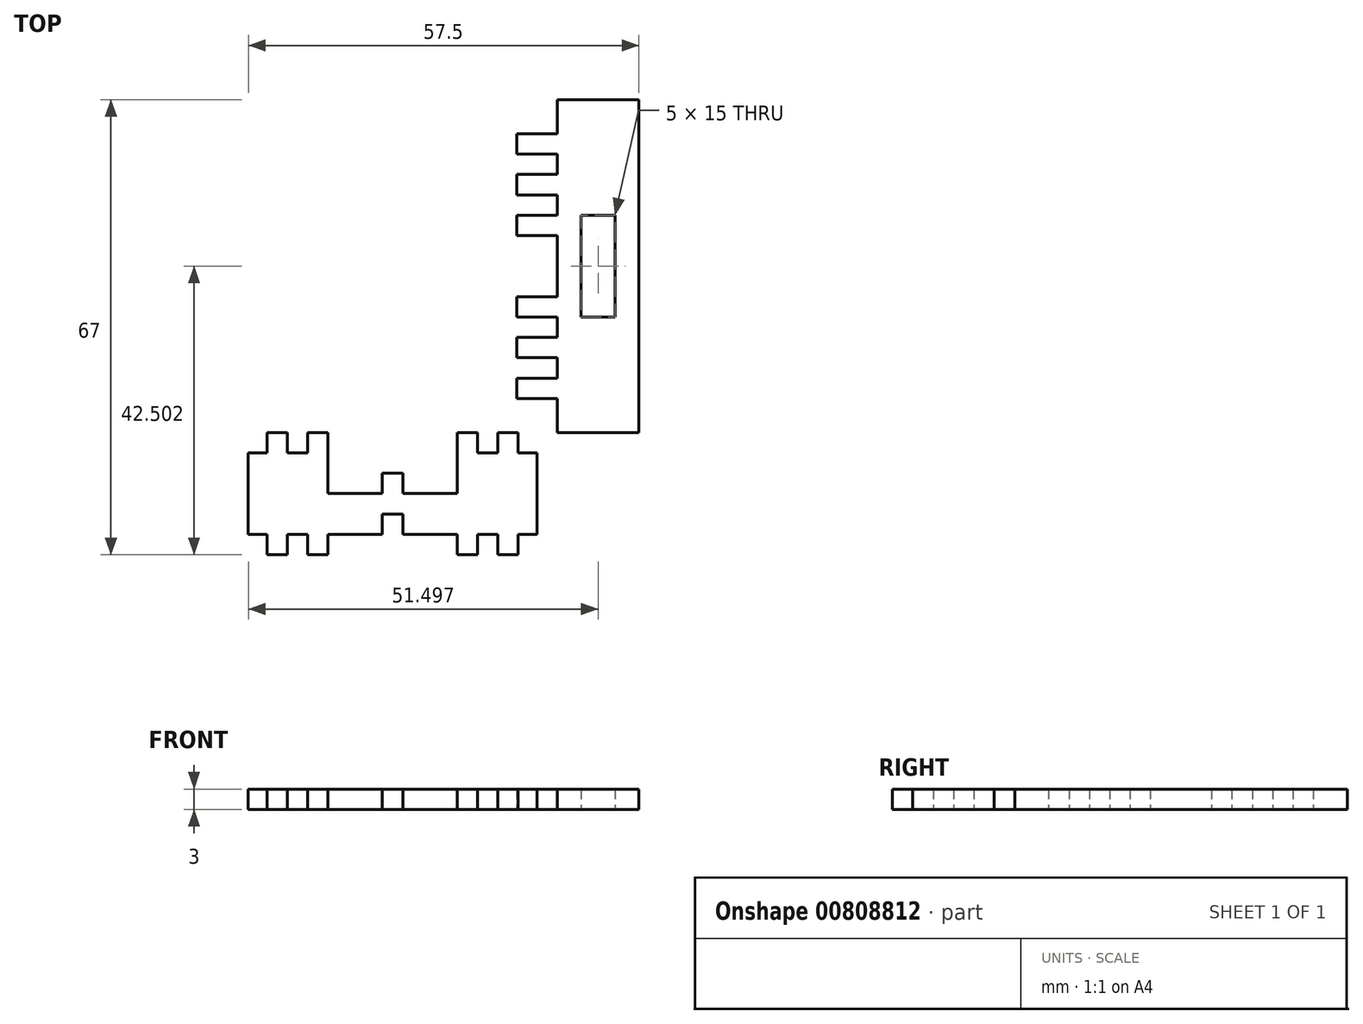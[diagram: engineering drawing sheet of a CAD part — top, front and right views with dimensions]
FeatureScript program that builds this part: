
annotation { "Feature Type Name" : "Feature", "Feature Type Description" : "" }
export const myFeature = defineFeature(function(context is Context, id is Id, definition is map)
    precondition{}
    {
        {
            var Q0;
            Q0=qCreatedBy(makeId("Top.planeOp"),FACE);
            var sketch = newSketch(context, id + "F0", { "sketchPlane" : qUnion([Q0])});
            skLineSegment(sketch, "E0.bottom", {"start": v(20.27, -26.13) * mm, "end": v(-22.23, -26.13) * mm});
            skLineSegment(sketch, "E0.top", {"start": v(20.27, 28.87) * mm, "end": v(-22.23, 28.87) * mm});
            skLineSegment(sketch, "E0.left", {"start": v(20.27, -26.13) * mm, "end": v(20.27, 28.87) * mm});
            skLineSegment(sketch, "E0.right", {"start": v(-22.23, -26.13) * mm, "end": v(-22.23, 28.87) * mm});
            skPoint(sketch, "E0.middle", {"position": v(-0.98, 1.37) * mm});
            skLineSegment(sketch, "E1.bottom", {"start": v(-19.23, -0.13) * mm, "end": v(-25.23, -0.13) * mm});
            skLineSegment(sketch, "E1.top", {"start": v(-19.23, 2.87) * mm, "end": v(-25.23, 2.87) * mm});
            skLineSegment(sketch, "E1.left", {"start": v(-19.23, -0.13) * mm, "end": v(-19.23, 2.87) * mm});
            skLineSegment(sketch, "E1.right", {"start": v(-25.23, -0.13) * mm, "end": v(-25.23, 2.87) * mm});
            skPoint(sketch, "E1.middle", {"position": v(-22.23, 1.37) * mm});
            skLineSegment(sketch, "E2.bottom", {"start": v(23.27, -0.13) * mm, "end": v(17.27, -0.13) * mm});
            skLineSegment(sketch, "E2.top", {"start": v(23.27, 2.87) * mm, "end": v(17.27, 2.87) * mm});
            skLineSegment(sketch, "E2.left", {"start": v(23.27, -0.13) * mm, "end": v(23.27, 2.87) * mm});
            skLineSegment(sketch, "E2.right", {"start": v(17.27, -0.13) * mm, "end": v(17.27, 2.87) * mm});
            skPoint(sketch, "E2.middle", {"position": v(20.27, 1.37) * mm});
            skLineSegment(sketch, "E3.bottom", {"start": v(0.52, -29.13) * mm, "end": v(-2.48, -29.13) * mm});
            skLineSegment(sketch, "E3.top", {"start": v(0.52, -23.13) * mm, "end": v(-2.48, -23.13) * mm});
            skLineSegment(sketch, "E3.left", {"start": v(0.52, -29.13) * mm, "end": v(0.52, -23.13) * mm});
            skLineSegment(sketch, "E3.right", {"start": v(-2.48, -29.13) * mm, "end": v(-2.48, -23.13) * mm});
            skPoint(sketch, "E3.middle", {"position": v(-0.98, -26.13) * mm});
            skLineSegment(sketch, "E4.bottom", {"start": v(0.52, 25.87) * mm, "end": v(-2.48, 25.87) * mm});
            skLineSegment(sketch, "E4.top", {"start": v(0.52, 31.87) * mm, "end": v(-2.48, 31.87) * mm});
            skLineSegment(sketch, "E4.left", {"start": v(0.52, 25.87) * mm, "end": v(0.52, 31.87) * mm});
            skLineSegment(sketch, "E4.right", {"start": v(-2.48, 25.87) * mm, "end": v(-2.48, 31.87) * mm});
            skPoint(sketch, "E4.middle", {"position": v(-0.98, 28.87) * mm});
            skLineSegment(sketch, "E5.bottom", {"start": v(-10.68, -18.58) * mm, "end": v(8.72, -18.58) * mm});
            skLineSegment(sketch, "E5.top", {"start": v(-10.68, 21.32) * mm, "end": v(8.72, 21.32) * mm});
            skLineSegment(sketch, "E5.left", {"start": v(-10.68, -18.58) * mm, "end": v(-10.68, 21.32) * mm});
            skLineSegment(sketch, "E5.right", {"start": v(8.72, -18.58) * mm, "end": v(8.72, 21.32) * mm});
            skLineSegment(sketch, "E6.bottom", {"start": v(-19.23, -6.13) * mm, "end": v(-25.23, -6.13) * mm});
            skLineSegment(sketch, "E6.top", {"start": v(-19.23, -3.13) * mm, "end": v(-25.23, -3.13) * mm});
            skLineSegment(sketch, "E6.left", {"start": v(-19.23, -6.13) * mm, "end": v(-19.23, -3.13) * mm});
            skLineSegment(sketch, "E6.right", {"start": v(-25.23, -6.13) * mm, "end": v(-25.23, -3.13) * mm});
            skPoint(sketch, "E6.middle", {"position": v(-22.23, -4.63) * mm});
            skLineSegment(sketch, "E7.bottom", {"start": v(-19.23, 5.87) * mm, "end": v(-25.23, 5.87) * mm});
            skLineSegment(sketch, "E7.top", {"start": v(-19.23, 8.87) * mm, "end": v(-25.23, 8.87) * mm});
            skLineSegment(sketch, "E7.left", {"start": v(-19.23, 5.87) * mm, "end": v(-19.23, 8.87) * mm});
            skLineSegment(sketch, "E7.right", {"start": v(-25.23, 5.87) * mm, "end": v(-25.23, 8.87) * mm});
            skPoint(sketch, "E7.middle", {"position": v(-22.23, 7.37) * mm});
            skLineSegment(sketch, "E8.bottom", {"start": v(-19.23, 11.87) * mm, "end": v(-25.23, 11.87) * mm});
            skLineSegment(sketch, "E8.top", {"start": v(-19.23, 14.87) * mm, "end": v(-25.23, 14.87) * mm});
            skLineSegment(sketch, "E8.left", {"start": v(-19.23, 11.87) * mm, "end": v(-19.23, 14.87) * mm});
            skLineSegment(sketch, "E8.right", {"start": v(-25.23, 11.87) * mm, "end": v(-25.23, 14.87) * mm});
            skPoint(sketch, "E8.middle", {"position": v(-22.23, 13.37) * mm});
            skLineSegment(sketch, "E9.bottom", {"start": v(-19.23, -12.13) * mm, "end": v(-25.23, -12.13) * mm});
            skLineSegment(sketch, "E9.top", {"start": v(-19.23, -9.13) * mm, "end": v(-25.23, -9.13) * mm});
            skLineSegment(sketch, "E9.left", {"start": v(-19.23, -12.13) * mm, "end": v(-19.23, -9.13) * mm});
            skLineSegment(sketch, "E9.right", {"start": v(-25.23, -12.13) * mm, "end": v(-25.23, -9.13) * mm});
            skPoint(sketch, "E9.middle", {"position": v(-22.23, -10.63) * mm});
            skLineSegment(sketch, "E10.bottom", {"start": v(-19.23, 17.87) * mm, "end": v(-25.23, 17.87) * mm});
            skLineSegment(sketch, "E10.top", {"start": v(-19.23, 20.87) * mm, "end": v(-25.23, 20.87) * mm});
            skLineSegment(sketch, "E10.left", {"start": v(-19.23, 17.87) * mm, "end": v(-19.23, 20.87) * mm});
            skLineSegment(sketch, "E10.right", {"start": v(-25.23, 17.87) * mm, "end": v(-25.23, 20.87) * mm});
            skPoint(sketch, "E10.middle", {"position": v(-22.23, 19.37) * mm});
            skLineSegment(sketch, "E11.bottom", {"start": v(-19.23, -18.13) * mm, "end": v(-25.23, -18.13) * mm});
            skLineSegment(sketch, "E11.top", {"start": v(-19.23, -15.13) * mm, "end": v(-25.23, -15.13) * mm});
            skLineSegment(sketch, "E11.left", {"start": v(-19.23, -18.13) * mm, "end": v(-19.23, -15.13) * mm});
            skLineSegment(sketch, "E11.right", {"start": v(-25.23, -18.13) * mm, "end": v(-25.23, -15.13) * mm});
            skPoint(sketch, "E11.middle", {"position": v(-22.23, -16.63) * mm});
            skLineSegment(sketch, "E12", {"start": v(-0.98, 1.37) * mm, "end": v(-0.98, 4.83) * mm});
            skLineSegment(sketch, "E13.MirrorCS", {"start": v(23.27, 5.87) * mm, "end": v(23.27, 8.87) * mm});
            skLineSegment(sketch, "E14.MirrorCS", {"start": v(23.27, -12.13) * mm, "end": v(23.27, -9.13) * mm});
            skLineSegment(sketch, "E15.MirrorCS", {"start": v(17.27, -12.13) * mm, "end": v(17.27, -9.13) * mm});
            skLineSegment(sketch, "E16.MirrorCS", {"start": v(17.27, 11.87) * mm, "end": v(17.27, 14.87) * mm});
            skLineSegment(sketch, "E17.MirrorCS", {"start": v(17.27, 5.87) * mm, "end": v(17.27, 8.87) * mm});
            skLineSegment(sketch, "E18.MirrorCS", {"start": v(17.27, 17.87) * mm, "end": v(17.27, 20.87) * mm});
            skLineSegment(sketch, "E19.MirrorCS", {"start": v(23.27, 11.87) * mm, "end": v(23.27, 14.87) * mm});
            skLineSegment(sketch, "E20.MirrorCS", {"start": v(23.27, 17.87) * mm, "end": v(23.27, 20.87) * mm});
            skLineSegment(sketch, "E21.MirrorCS", {"start": v(17.27, 11.87) * mm, "end": v(23.27, 11.87) * mm});
            skLineSegment(sketch, "E22.MirrorCS", {"start": v(17.27, -3.13) * mm, "end": v(23.27, -3.13) * mm});
            skLineSegment(sketch, "E23.MirrorCS", {"start": v(17.27, 20.87) * mm, "end": v(23.27, 20.87) * mm});
            skLineSegment(sketch, "E24.MirrorCS", {"start": v(17.27, -0.13) * mm, "end": v(23.27, -0.13) * mm});
            skLineSegment(sketch, "E25.MirrorCS", {"start": v(17.27, 2.87) * mm, "end": v(23.27, 2.87) * mm});
            skLineSegment(sketch, "E26.MirrorCS", {"start": v(17.27, 17.87) * mm, "end": v(23.27, 17.87) * mm});
            skLineSegment(sketch, "E27.MirrorCS", {"start": v(17.27, 14.87) * mm, "end": v(23.27, 14.87) * mm});
            skLineSegment(sketch, "E28.MirrorCS", {"start": v(17.27, -9.13) * mm, "end": v(23.27, -9.13) * mm});
            skLineSegment(sketch, "E29.MirrorCS", {"start": v(17.27, 5.87) * mm, "end": v(23.27, 5.87) * mm});
            skLineSegment(sketch, "E30.MirrorCS", {"start": v(17.27, -18.13) * mm, "end": v(23.27, -18.13) * mm});
            skLineSegment(sketch, "E31.MirrorCS", {"start": v(17.27, 8.87) * mm, "end": v(23.27, 8.87) * mm});
            skLineSegment(sketch, "E32.MirrorCS", {"start": v(17.27, -12.13) * mm, "end": v(23.27, -12.13) * mm});
            skLineSegment(sketch, "E33.MirrorCS", {"start": v(23.27, -18.13) * mm, "end": v(23.27, -15.13) * mm});
            skLineSegment(sketch, "E34.MirrorCS", {"start": v(17.27, -6.13) * mm, "end": v(23.27, -6.13) * mm});
            skPoint(sketch, "E35.MirrorP", {"position": v(20.27, -4.63) * mm});
            skPoint(sketch, "E36.MirrorP", {"position": v(20.27, 7.37) * mm});
            skLineSegment(sketch, "E37.MirrorCS", {"start": v(17.27, -18.13) * mm, "end": v(17.27, -15.13) * mm});
            skPoint(sketch, "E38.MirrorP", {"position": v(20.27, 19.37) * mm});
            skLineSegment(sketch, "E39.MirrorCS", {"start": v(17.27, -6.13) * mm, "end": v(17.27, -3.13) * mm});
            skPoint(sketch, "E40.MirrorP", {"position": v(20.27, 13.37) * mm});
            skLineSegment(sketch, "E41.MirrorCS", {"start": v(17.27, -15.13) * mm, "end": v(23.27, -15.13) * mm});
            skPoint(sketch, "E42.MirrorP", {"position": v(20.27, -10.63) * mm});
            skLineSegment(sketch, "E43.MirrorCS", {"start": v(23.27, -6.13) * mm, "end": v(23.27, -3.13) * mm});
            skPoint(sketch, "E44.MirrorP", {"position": v(20.27, -16.63) * mm});
            skCircle(sketch, "E45", {"center": v(4.02, 25.37) * mm, "radius": 1.65 * mm});
            skCircle(sketch, "E46", {"center": v(-5.98, 25.37) * mm, "radius": 1.65 * mm});
            skCircle(sketch, "E47", {"center": v(-5.98, -22.63) * mm, "radius": 1.65 * mm});
            skCircle(sketch, "E48", {"center": v(4.02, -22.63) * mm, "radius": 1.65 * mm});
            skLineSegment(sketch, "E49.bottom", {"start": v(-13.48, 25.87) * mm, "end": v(-10.48, 25.87) * mm});
            skLineSegment(sketch, "E49.top", {"start": v(-13.48, 31.87) * mm, "end": v(-10.48, 31.87) * mm});
            skLineSegment(sketch, "E49.left", {"start": v(-13.48, 25.87) * mm, "end": v(-13.48, 31.87) * mm});
            skLineSegment(sketch, "E49.right", {"start": v(-10.48, 25.87) * mm, "end": v(-10.48, 31.87) * mm});
            skPoint(sketch, "E49.middle", {"position": v(-11.98, 28.87) * mm});
            skLineSegment(sketch, "E50.bottom", {"start": v(-16.48, 25.87) * mm, "end": v(-19.48, 25.87) * mm});
            skLineSegment(sketch, "E50.top", {"start": v(-16.48, 31.87) * mm, "end": v(-19.48, 31.87) * mm});
            skLineSegment(sketch, "E50.left", {"start": v(-16.48, 25.87) * mm, "end": v(-16.48, 31.87) * mm});
            skLineSegment(sketch, "E50.right", {"start": v(-19.48, 25.87) * mm, "end": v(-19.48, 31.87) * mm});
            skPoint(sketch, "E50.middle", {"position": v(-17.98, 28.87) * mm});
            skLineSegment(sketch, "E51.MirrorCS", {"start": v(8.52, 25.87) * mm, "end": v(8.52, 31.87) * mm});
            skLineSegment(sketch, "E52.MirrorCS", {"start": v(11.52, 31.87) * mm, "end": v(8.52, 31.87) * mm});
            skLineSegment(sketch, "E53.MirrorCS", {"start": v(11.52, 25.87) * mm, "end": v(11.52, 31.87) * mm});
            skLineSegment(sketch, "E54.MirrorCS", {"start": v(11.52, 25.87) * mm, "end": v(8.52, 25.87) * mm});
            skLineSegment(sketch, "E55.MirrorCS", {"start": v(14.52, 25.87) * mm, "end": v(17.52, 25.87) * mm});
            skLineSegment(sketch, "E56.MirrorCS", {"start": v(14.52, 25.87) * mm, "end": v(14.52, 31.87) * mm});
            skLineSegment(sketch, "E57.MirrorCS", {"start": v(14.52, 31.87) * mm, "end": v(17.52, 31.87) * mm});
            skLineSegment(sketch, "E58.MirrorCS", {"start": v(17.52, 25.87) * mm, "end": v(17.52, 31.87) * mm});
            skPoint(sketch, "E59.MirrorP", {"position": v(10.02, 28.87) * mm});
            skPoint(sketch, "E60.MirrorP", {"position": v(16.02, 28.87) * mm});
            skLineSegment(sketch, "E61", {"start": v(-0.98, 1.37) * mm, "end": v(4.17, 1.37) * mm});
            skLineSegment(sketch, "E62.MirrorCS", {"start": v(-16.48, -29.13) * mm, "end": v(-19.48, -29.13) * mm});
            skLineSegment(sketch, "E63.MirrorCS", {"start": v(-13.48, -29.13) * mm, "end": v(-10.48, -29.13) * mm});
            skLineSegment(sketch, "E64.MirrorCS", {"start": v(-16.48, -23.13) * mm, "end": v(-19.48, -23.13) * mm});
            skLineSegment(sketch, "E65.MirrorCS", {"start": v(14.52, -23.13) * mm, "end": v(17.52, -23.13) * mm});
            skLineSegment(sketch, "E66.MirrorCS", {"start": v(11.52, -23.13) * mm, "end": v(8.52, -23.13) * mm});
            skLineSegment(sketch, "E67.MirrorCS", {"start": v(11.52, -29.13) * mm, "end": v(8.52, -29.13) * mm});
            skLineSegment(sketch, "E68.MirrorCS", {"start": v(14.52, -29.13) * mm, "end": v(17.52, -29.13) * mm});
            skLineSegment(sketch, "E69.MirrorCS", {"start": v(-13.48, -23.13) * mm, "end": v(-10.48, -23.13) * mm});
            skLineSegment(sketch, "E70.MirrorCS", {"start": v(-10.48, -23.13) * mm, "end": v(-10.48, -29.13) * mm});
            skLineSegment(sketch, "E71.MirrorCS", {"start": v(-19.48, -23.13) * mm, "end": v(-19.48, -29.13) * mm});
            skLineSegment(sketch, "E72.MirrorCS", {"start": v(8.52, -23.13) * mm, "end": v(8.52, -29.13) * mm});
            skLineSegment(sketch, "E73.MirrorCS", {"start": v(-16.48, -23.13) * mm, "end": v(-16.48, -29.13) * mm});
            skLineSegment(sketch, "E74.MirrorCS", {"start": v(11.52, -23.13) * mm, "end": v(11.52, -29.13) * mm});
            skLineSegment(sketch, "E75.MirrorCS", {"start": v(-13.48, -23.13) * mm, "end": v(-13.48, -29.13) * mm});
            skLineSegment(sketch, "E76.MirrorCS", {"start": v(20.27, 28.87) * mm, "end": v(20.27, -26.13) * mm});
            skLineSegment(sketch, "E77.MirrorCS", {"start": v(14.52, -23.13) * mm, "end": v(14.52, -29.13) * mm});
            skLineSegment(sketch, "E78.MirrorCS", {"start": v(17.52, -23.13) * mm, "end": v(17.52, -29.13) * mm});
            skLineSegment(sketch, "E79.MirrorCS", {"start": v(-2.48, -23.13) * mm, "end": v(-2.48, -29.13) * mm});
            skLineSegment(sketch, "E80.MirrorCS", {"start": v(0.52, -23.13) * mm, "end": v(0.52, -29.13) * mm});
            skPoint(sketch, "E81.MirrorP", {"position": v(10.02, -26.13) * mm});
            skPoint(sketch, "E82.MirrorP", {"position": v(-17.98, -26.13) * mm});
            skPoint(sketch, "E83.MirrorP", {"position": v(-11.98, -26.13) * mm});
            skPoint(sketch, "E84.MirrorP", {"position": v(16.02, -26.13) * mm});
            skLineSegment(sketch, "E85.MirrorCS", {"start": v(-22.23, 28.87) * mm, "end": v(-22.23, -26.13) * mm});
            skLineSegment(sketch, "E86.bottom", {"start": v(23.27, 25.87) * mm, "end": v(35.27, 25.87) * mm});
            skLineSegment(sketch, "E86.top", {"start": v(23.27, -23.13) * mm, "end": v(35.27, -23.13) * mm});
            skLineSegment(sketch, "E86.left", {"start": v(23.27, 25.87) * mm, "end": v(23.27, -23.13) * mm});
            skLineSegment(sketch, "E86.right", {"start": v(35.27, 25.87) * mm, "end": v(35.27, -23.13) * mm});
            skLineSegment(sketch, "E87", {"start": v(29.27, 25.87) * mm, "end": v(29.27, 16.55) * mm});
            skPoint(sketch, "E87.endSnap0", {"position": v(29.27, 25.87) * mm});
            skLineSegment(sketch, "E88.MirrorCS", {"start": v(41.27, 2.87) * mm, "end": v(35.27, 2.87) * mm});
            skLineSegment(sketch, "E89.MirrorCS", {"start": v(35.27, 2.87) * mm, "end": v(41.27, 2.87) * mm});
            skLineSegment(sketch, "E90.MirrorCS", {"start": v(41.27, -9.13) * mm, "end": v(35.27, -9.13) * mm});
            skLineSegment(sketch, "E91.MirrorCS", {"start": v(41.27, 14.87) * mm, "end": v(35.27, 14.87) * mm});
            skLineSegment(sketch, "E92.MirrorCS", {"start": v(41.27, 8.87) * mm, "end": v(35.27, 8.87) * mm});
            skLineSegment(sketch, "E93.MirrorCS", {"start": v(41.27, -0.13) * mm, "end": v(41.27, 2.87) * mm});
            skLineSegment(sketch, "E94.MirrorCS", {"start": v(35.27, -0.13) * mm, "end": v(35.27, 2.87) * mm});
            skPoint(sketch, "E95.MirrorP", {"position": v(38.27, 1.37) * mm});
            skLineSegment(sketch, "E96.MirrorCS", {"start": v(41.27, 20.87) * mm, "end": v(35.27, 20.87) * mm});
            skLineSegment(sketch, "E97.MirrorCS", {"start": v(41.27, -3.13) * mm, "end": v(35.27, -3.13) * mm});
            skLineSegment(sketch, "E98.MirrorCS", {"start": v(41.27, -15.13) * mm, "end": v(35.27, -15.13) * mm});
            skLineSegment(sketch, "E99.MirrorCS", {"start": v(41.27, -0.13) * mm, "end": v(35.27, -0.13) * mm});
            skLineSegment(sketch, "E100.MirrorCS", {"start": v(35.27, -12.13) * mm, "end": v(35.27, -9.13) * mm});
            skLineSegment(sketch, "E101.MirrorCS", {"start": v(41.27, 5.87) * mm, "end": v(35.27, 5.87) * mm});
            skLineSegment(sketch, "E102.MirrorCS", {"start": v(41.27, -12.13) * mm, "end": v(41.27, -9.13) * mm});
            skPoint(sketch, "E103.MirrorP", {"position": v(38.27, -4.63) * mm});
            skLineSegment(sketch, "E104.MirrorCS", {"start": v(41.27, -18.13) * mm, "end": v(35.27, -18.13) * mm});
            skLineSegment(sketch, "E105.MirrorCS", {"start": v(41.27, 11.87) * mm, "end": v(41.27, 14.87) * mm});
            skLineSegment(sketch, "E106.MirrorCS", {"start": v(35.27, 5.87) * mm, "end": v(35.27, 8.87) * mm});
            skPoint(sketch, "E107.MirrorP", {"position": v(38.27, 7.37) * mm});
            skPoint(sketch, "E108.MirrorP", {"position": v(38.27, 19.37) * mm});
            skLineSegment(sketch, "E109.MirrorCS", {"start": v(41.27, -12.13) * mm, "end": v(35.27, -12.13) * mm});
            skLineSegment(sketch, "E110.MirrorCS", {"start": v(41.27, 5.87) * mm, "end": v(41.27, 8.87) * mm});
            skLineSegment(sketch, "E111.MirrorCS", {"start": v(35.27, -18.13) * mm, "end": v(35.27, -15.13) * mm});
            skPoint(sketch, "E112.MirrorP", {"position": v(38.27, 13.37) * mm});
            skLineSegment(sketch, "E113.MirrorCS", {"start": v(41.27, 17.87) * mm, "end": v(41.27, 20.87) * mm});
            skLineSegment(sketch, "E114.MirrorCS", {"start": v(41.27, -6.13) * mm, "end": v(35.27, -6.13) * mm});
            skPoint(sketch, "E115.MirrorP", {"position": v(38.27, -10.63) * mm});
            skLineSegment(sketch, "E116.MirrorCS", {"start": v(35.27, 11.87) * mm, "end": v(35.27, 14.87) * mm});
            skLineSegment(sketch, "E117.MirrorCS", {"start": v(35.27, 17.87) * mm, "end": v(35.27, 20.87) * mm});
            skLineSegment(sketch, "E118.MirrorCS", {"start": v(41.27, -18.13) * mm, "end": v(41.27, -15.13) * mm});
            skPoint(sketch, "E119.MirrorP", {"position": v(38.27, -16.63) * mm});
            skLineSegment(sketch, "E120.MirrorCS", {"start": v(41.27, 11.87) * mm, "end": v(35.27, 11.87) * mm});
            skLineSegment(sketch, "E121.MirrorCS", {"start": v(41.27, -6.13) * mm, "end": v(41.27, -3.13) * mm});
            skLineSegment(sketch, "E122.MirrorCS", {"start": v(35.27, -6.13) * mm, "end": v(35.27, -3.13) * mm});
            skLineSegment(sketch, "E123.MirrorCS", {"start": v(35.27, -0.13) * mm, "end": v(41.27, -0.13) * mm});
            skLineSegment(sketch, "E124.MirrorCS", {"start": v(41.27, 17.87) * mm, "end": v(35.27, 17.87) * mm});
            skLineSegment(sketch, "E125.MirrorCS", {"start": v(38.27, -26.13) * mm, "end": v(38.27, 28.87) * mm});
            skLineSegment(sketch, "E126", {"start": v(-22.23, -26.13) * mm, "end": v(-22.23, -38.13) * mm});
            skLineSegment(sketch, "E127", {"start": v(-22.23, -38.13) * mm, "end": v(20.27, -38.13) * mm});
            skLineSegment(sketch, "E128", {"start": v(20.27, -38.13) * mm, "end": v(20.27, -26.13) * mm});
            skLineSegment(sketch, "E129", {"start": v(-22.23, -32.13) * mm, "end": v(-17, -32.13) * mm});
            skLineSegment(sketch, "E130", {"start": v(-10.48, -29.13) * mm, "end": v(-10.48, -32.13) * mm});
            skLineSegment(sketch, "E131", {"start": v(-10.48, -32.13) * mm, "end": v(-2.48, -32.13) * mm});
            skLineSegment(sketch, "E132", {"start": v(-2.48, -32.13) * mm, "end": v(-2.48, -29.13) * mm});
            skLineSegment(sketch, "E133", {"start": v(0.52, -27.61) * mm, "end": v(0.52, -32.13) * mm});
            skLineSegment(sketch, "E134", {"start": v(0.52, -32.13) * mm, "end": v(8.52, -32.13) * mm});
            skLineSegment(sketch, "E135", {"start": v(8.52, -32.13) * mm, "end": v(8.52, -29.13) * mm});
            skLineSegment(sketch, "E136.MirrorCS", {"start": v(-2.48, -41.13) * mm, "end": v(-2.48, -35.13) * mm});
            skLineSegment(sketch, "E137.MirrorCS", {"start": v(0.52, -41.13) * mm, "end": v(0.52, -35.13) * mm});
            skLineSegment(sketch, "E138.MirrorCS", {"start": v(0.52, -41.13) * mm, "end": v(-2.48, -41.13) * mm});
            skLineSegment(sketch, "E139.MirrorCS", {"start": v(0.52, -35.13) * mm, "end": v(-2.48, -35.13) * mm});
            skPoint(sketch, "E140.MirrorP", {"position": v(-0.98, -38.13) * mm});
            skLineSegment(sketch, "E141.MirrorCS", {"start": v(-13.48, -41.13) * mm, "end": v(-13.48, -35.13) * mm});
            skLineSegment(sketch, "E142.MirrorCS", {"start": v(-16.48, -35.13) * mm, "end": v(-19.48, -35.13) * mm});
            skLineSegment(sketch, "E143.MirrorCS", {"start": v(14.52, -41.13) * mm, "end": v(14.52, -35.13) * mm});
            skLineSegment(sketch, "E144.MirrorCS", {"start": v(-13.48, -35.13) * mm, "end": v(-10.48, -35.13) * mm});
            skLineSegment(sketch, "E145.MirrorCS", {"start": v(17.52, -41.13) * mm, "end": v(17.52, -35.13) * mm});
            skLineSegment(sketch, "E146.MirrorCS", {"start": v(-16.48, -41.13) * mm, "end": v(-19.48, -41.13) * mm});
            skLineSegment(sketch, "E147.MirrorCS", {"start": v(11.52, -41.13) * mm, "end": v(11.52, -35.13) * mm});
            skLineSegment(sketch, "E148.MirrorCS", {"start": v(14.52, -41.13) * mm, "end": v(17.52, -41.13) * mm});
            skLineSegment(sketch, "E149.MirrorCS", {"start": v(11.52, -41.13) * mm, "end": v(8.52, -41.13) * mm});
            skPoint(sketch, "E150.MirrorP", {"position": v(10.02, -38.13) * mm});
            skLineSegment(sketch, "E151.MirrorCS", {"start": v(11.52, -35.13) * mm, "end": v(8.52, -35.13) * mm});
            skLineSegment(sketch, "E152.MirrorCS", {"start": v(14.52, -35.13) * mm, "end": v(17.52, -35.13) * mm});
            skPoint(sketch, "E153.MirrorP", {"position": v(16.02, -38.13) * mm});
            skLineSegment(sketch, "E154.MirrorCS", {"start": v(-10.48, -41.13) * mm, "end": v(-10.48, -35.13) * mm});
            skPoint(sketch, "E155.MirrorP", {"position": v(-17.98, -38.13) * mm});
            skLineSegment(sketch, "E156.MirrorCS", {"start": v(-13.48, -41.13) * mm, "end": v(-10.48, -41.13) * mm});
            skLineSegment(sketch, "E157.MirrorCS", {"start": v(-19.48, -41.13) * mm, "end": v(-19.48, -35.13) * mm});
            skPoint(sketch, "E158.MirrorP", {"position": v(-11.98, -38.13) * mm});
            skLineSegment(sketch, "E159.MirrorCS", {"start": v(8.52, -41.13) * mm, "end": v(8.52, -35.13) * mm});
            skLineSegment(sketch, "E160.MirrorCS", {"start": v(0.52, -35.13) * mm, "end": v(0.52, -41.13) * mm});
            skLineSegment(sketch, "E161.MirrorCS", {"start": v(-2.48, -35.13) * mm, "end": v(-2.48, -41.13) * mm});
            skLineSegment(sketch, "E162.MirrorCS", {"start": v(-16.48, -41.13) * mm, "end": v(-16.48, -35.13) * mm});
            skSolve(sketch);
        }
        {
            var Q0;
            {var subQ9=sQuery(id+"F0.wireOp",EDGE,"E86.top");Q0=makeQuery(id+"F0.imprint","IMPRINT",FACE,{"disambiguationData":[TD([[makeQuery(id+"F0.imprint","IMPRINT",EDGE,{"derivedFrom":subQ9}),1.0]])]});}
            var Q1;
            {var subQ0=sQuery(id+"F0.wireOp",EDGE,"E100.MirrorCS");Q1=makeQuery(id+"F0.imprint","IMPRINT",FACE,{"disambiguationData":[TD([[makeQuery(id+"F0.imprint","IMPRINT",EDGE,{"derivedFrom":subQ0}),-1.0]])]});}
            var Q2;
            {var subQ0=sQuery(id+"F0.wireOp",EDGE,"E111.MirrorCS");Q2=makeQuery(id+"F0.imprint","IMPRINT",FACE,{"disambiguationData":[TD([[makeQuery(id+"F0.imprint","IMPRINT",EDGE,{"derivedFrom":subQ0}),-1.0]])]});}
            var Q3;
            {var subQ0=sQuery(id+"F0.wireOp",EDGE,"E122.MirrorCS");Q3=makeQuery(id+"F0.imprint","IMPRINT",FACE,{"disambiguationData":[TD([[makeQuery(id+"F0.imprint","IMPRINT",EDGE,{"derivedFrom":subQ0}),-1.0]])]});}
            var Q4;
            {var subQ0=sQuery(id+"F0.wireOp",EDGE,"E94.MirrorCS");Q4=makeQuery(id+"F0.imprint","IMPRINT",FACE,{"disambiguationData":[TD([[makeQuery(id+"F0.imprint","IMPRINT",EDGE,{"derivedFrom":subQ0}),-1.0]])]});}
            var Q5;
            {var subQ0=sQuery(id+"F0.wireOp",EDGE,"E106.MirrorCS");Q5=makeQuery(id+"F0.imprint","IMPRINT",FACE,{"disambiguationData":[TD([[makeQuery(id+"F0.imprint","IMPRINT",EDGE,{"derivedFrom":subQ0}),-1.0]])]});}
            var Q6;
            {var subQ0=sQuery(id+"F0.wireOp",EDGE,"E116.MirrorCS");Q6=makeQuery(id+"F0.imprint","IMPRINT",FACE,{"disambiguationData":[TD([[makeQuery(id+"F0.imprint","IMPRINT",EDGE,{"derivedFrom":subQ0}),-1.0]])]});}
            var Q7;
            {var subQ0=sQuery(id+"F0.wireOp",EDGE,"E117.MirrorCS");Q7=makeQuery(id+"F0.imprint","IMPRINT",FACE,{"disambiguationData":[TD([[makeQuery(id+"F0.imprint","IMPRINT",EDGE,{"derivedFrom":subQ0}),-1.0]])]});}
            var Q8;
            {var subQ0=sQuery(id+"F0.wireOp",EDGE,"E86.left");var subQ1=sQuery(id+"F0.wireOp",EDGE,"E23.MirrorCS");var subQ2=makeQuery(id+"F0.imprint","INTERSECT",VERTEX,{"derivedFrom":[subQ1,subQ0]});Q8=makeQuery(id+"F0.imprint","IMPRINT",FACE,{"disambiguationData":[TD([[makeQuery(id+"F0.imprint","IMPRINT",EDGE,{"disambiguationData":[TD([[subQ2,1.0]])],"derivedFrom":subQ1}),-1.0]])]});}
            var Q9;
            {var subQ0=sQuery(id+"F0.wireOp",EDGE,"E18.MirrorCS");Q9=makeQuery(id+"F0.imprint","IMPRINT",FACE,{"disambiguationData":[TD([[makeQuery(id+"F0.imprint","IMPRINT",EDGE,{"derivedFrom":subQ0}),-1.0]])]});}
            var Q10;
            {var subQ0=sQuery(id+"F0.wireOp",EDGE,"E16.MirrorCS");Q10=makeQuery(id+"F0.imprint","IMPRINT",FACE,{"disambiguationData":[TD([[makeQuery(id+"F0.imprint","IMPRINT",EDGE,{"derivedFrom":subQ0}),-1.0]])]});}
            var Q11;
            {var subQ0=sQuery(id+"F0.wireOp",EDGE,"E86.left");var subQ1=sQuery(id+"F0.wireOp",EDGE,"E21.MirrorCS");var subQ2=makeQuery(id+"F0.imprint","INTERSECT",VERTEX,{"derivedFrom":[subQ1,subQ0]});Q11=makeQuery(id+"F0.imprint","IMPRINT",FACE,{"disambiguationData":[TD([[makeQuery(id+"F0.imprint","IMPRINT",EDGE,{"disambiguationData":[TD([[subQ2,1.0]])],"derivedFrom":subQ1}),1.0]])]});}
            var Q12;
            {var subQ0=sQuery(id+"F0.wireOp",EDGE,"E86.left");var subQ1=sQuery(id+"F0.wireOp",EDGE,"E29.MirrorCS");var subQ2=makeQuery(id+"F0.imprint","INTERSECT",VERTEX,{"derivedFrom":[subQ1,subQ0]});Q12=makeQuery(id+"F0.imprint","IMPRINT",FACE,{"disambiguationData":[TD([[makeQuery(id+"F0.imprint","IMPRINT",EDGE,{"disambiguationData":[TD([[subQ2,1.0]])],"derivedFrom":subQ1}),1.0]])]});}
            var Q13;
            {var subQ0=sQuery(id+"F0.wireOp",EDGE,"E17.MirrorCS");Q13=makeQuery(id+"F0.imprint","IMPRINT",FACE,{"disambiguationData":[TD([[makeQuery(id+"F0.imprint","IMPRINT",EDGE,{"derivedFrom":subQ0}),-1.0]])]});}
            var Q14;
            {var subQ0=sQuery(id+"F0.wireOp",EDGE,"E2.right");Q14=makeQuery(id+"F0.imprint","IMPRINT",FACE,{"disambiguationData":[TD([[makeQuery(id+"F0.imprint","IMPRINT",EDGE,{"derivedFrom":subQ0}),-1.0]])]});}
            var Q15;
            {var subQ0=sQuery(id+"F0.wireOp",EDGE,"E86.left");var subQ1=sQuery(id+"F0.wireOp",EDGE,"E24.MirrorCS");var subQ2=makeQuery(id+"F0.imprint","INTERSECT",VERTEX,{"derivedFrom":[subQ1,subQ0]});Q15=makeQuery(id+"F0.imprint","IMPRINT",FACE,{"disambiguationData":[TD([[makeQuery(id+"F0.imprint","IMPRINT",EDGE,{"disambiguationData":[TD([[subQ2,1.0]])],"derivedFrom":subQ1}),1.0]])]});}
            var Q16;
            {var subQ0=sQuery(id+"F0.wireOp",EDGE,"E39.MirrorCS");Q16=makeQuery(id+"F0.imprint","IMPRINT",FACE,{"disambiguationData":[TD([[makeQuery(id+"F0.imprint","IMPRINT",EDGE,{"derivedFrom":subQ0}),-1.0]])]});}
            var Q17;
            {var subQ0=sQuery(id+"F0.wireOp",EDGE,"E15.MirrorCS");Q17=makeQuery(id+"F0.imprint","IMPRINT",FACE,{"disambiguationData":[TD([[makeQuery(id+"F0.imprint","IMPRINT",EDGE,{"derivedFrom":subQ0}),-1.0]])]});}
            var Q18;
            {var subQ0=sQuery(id+"F0.wireOp",EDGE,"E86.left");var subQ1=sQuery(id+"F0.wireOp",EDGE,"E28.MirrorCS");var subQ2=makeQuery(id+"F0.imprint","INTERSECT",VERTEX,{"derivedFrom":[subQ1,subQ0]});Q18=makeQuery(id+"F0.imprint","IMPRINT",FACE,{"disambiguationData":[TD([[makeQuery(id+"F0.imprint","IMPRINT",EDGE,{"disambiguationData":[TD([[subQ2,1.0]])],"derivedFrom":subQ1}),-1.0]])]});}
            var Q19;
            {var subQ0=sQuery(id+"F0.wireOp",EDGE,"E86.left");var subQ1=sQuery(id+"F0.wireOp",EDGE,"E30.MirrorCS");var subQ2=makeQuery(id+"F0.imprint","INTERSECT",VERTEX,{"derivedFrom":[subQ1,subQ0]});Q19=makeQuery(id+"F0.imprint","IMPRINT",FACE,{"disambiguationData":[TD([[makeQuery(id+"F0.imprint","IMPRINT",EDGE,{"disambiguationData":[TD([[subQ2,1.0]])],"derivedFrom":subQ1}),1.0]])]});}
            var Q20;
            {var subQ0=sQuery(id+"F0.wireOp",EDGE,"E37.MirrorCS");Q20=makeQuery(id+"F0.imprint","IMPRINT",FACE,{"disambiguationData":[TD([[makeQuery(id+"F0.imprint","IMPRINT",EDGE,{"derivedFrom":subQ0}),-1.0]])]});}
            var Q21;
            {var subQ0=sQuery(id+"F0.wireOp",EDGE,"E66.MirrorCS");Q21=makeQuery(id+"F0.imprint","IMPRINT",FACE,{"disambiguationData":[TD([[makeQuery(id+"F0.imprint","IMPRINT",EDGE,{"derivedFrom":subQ0}),1.0]])]});}
            var Q22;
            {var subQ0=sQuery(id+"F0.wireOp",EDGE,"E67.MirrorCS");Q22=makeQuery(id+"F0.imprint","IMPRINT",FACE,{"disambiguationData":[TD([[makeQuery(id+"F0.imprint","IMPRINT",EDGE,{"derivedFrom":subQ0}),-1.0]])]});}
            var Q23;
            {var subQ0=sQuery(id+"F0.wireOp",EDGE,"E68.MirrorCS");Q23=makeQuery(id+"F0.imprint","IMPRINT",FACE,{"disambiguationData":[TD([[makeQuery(id+"F0.imprint","IMPRINT",EDGE,{"derivedFrom":subQ0}),1.0]])]});}
            var Q24;
            {var subQ0=sQuery(id+"F0.wireOp",EDGE,"E65.MirrorCS");Q24=makeQuery(id+"F0.imprint","IMPRINT",FACE,{"disambiguationData":[TD([[makeQuery(id+"F0.imprint","IMPRINT",EDGE,{"derivedFrom":subQ0}),-1.0]])]});}
            var Q25;
            {var subQ5=sQuery(id+"F0.wireOp",EDGE,"E152.MirrorCS");Q25=makeQuery(id+"F0.imprint","IMPRINT",FACE,{"disambiguationData":[TD([[makeQuery(id+"F0.imprint","IMPRINT",EDGE,{"derivedFrom":subQ5}),-1.0]])]});}
            var Q26;
            {var subQ5=sQuery(id+"F0.wireOp",EDGE,"E151.MirrorCS");Q26=makeQuery(id+"F0.imprint","IMPRINT",FACE,{"disambiguationData":[TD([[makeQuery(id+"F0.imprint","IMPRINT",EDGE,{"derivedFrom":subQ5}),1.0]])]});}
            var Q27;
            {var subQ5=sQuery(id+"F0.wireOp",EDGE,"E149.MirrorCS");Q27=makeQuery(id+"F0.imprint","IMPRINT",FACE,{"disambiguationData":[TD([[makeQuery(id+"F0.imprint","IMPRINT",EDGE,{"derivedFrom":subQ5}),-1.0]])]});}
            var Q28;
            {var subQ5=sQuery(id+"F0.wireOp",EDGE,"E148.MirrorCS");Q28=makeQuery(id+"F0.imprint","IMPRINT",FACE,{"disambiguationData":[TD([[makeQuery(id+"F0.imprint","IMPRINT",EDGE,{"derivedFrom":subQ5}),1.0]])]});}
            var Q29;
            {var subQ5=sQuery(id+"F0.wireOp",EDGE,"E138.MirrorCS");Q29=makeQuery(id+"F0.imprint","IMPRINT",FACE,{"disambiguationData":[TD([[makeQuery(id+"F0.imprint","IMPRINT",EDGE,{"derivedFrom":subQ5}),-1.0]])]});}
            var Q30;
            {var subQ5=sQuery(id+"F0.wireOp",EDGE,"E139.MirrorCS");Q30=makeQuery(id+"F0.imprint","IMPRINT",FACE,{"disambiguationData":[TD([[makeQuery(id+"F0.imprint","IMPRINT",EDGE,{"derivedFrom":subQ5}),1.0]])]});}
            var Q31;
            {var subQ7=sQuery(id+"F0.wireOp",EDGE,"E3.bottom");Q31=makeQuery(id+"F0.imprint","IMPRINT",FACE,{"disambiguationData":[TD([[makeQuery(id+"F0.imprint","IMPRINT",EDGE,{"derivedFrom":subQ7}),-1.0]])]});}
            var Q32;
            {var subQ0=sQuery(id+"F0.wireOp",EDGE,"E3.top");Q32=makeQuery(id+"F0.imprint","IMPRINT",FACE,{"disambiguationData":[TD([[makeQuery(id+"F0.imprint","IMPRINT",EDGE,{"derivedFrom":subQ0}),1.0]])]});}
            var Q33;
            {var subQ0=sQuery(id+"F0.wireOp",EDGE,"E69.MirrorCS");Q33=makeQuery(id+"F0.imprint","IMPRINT",FACE,{"disambiguationData":[TD([[makeQuery(id+"F0.imprint","IMPRINT",EDGE,{"derivedFrom":subQ0}),-1.0]])]});}
            var Q34;
            {var subQ0=sQuery(id+"F0.wireOp",EDGE,"E63.MirrorCS");Q34=makeQuery(id+"F0.imprint","IMPRINT",FACE,{"disambiguationData":[TD([[makeQuery(id+"F0.imprint","IMPRINT",EDGE,{"derivedFrom":subQ0}),1.0]])]});}
            var Q35;
            {var subQ5=sQuery(id+"F0.wireOp",EDGE,"E144.MirrorCS");Q35=makeQuery(id+"F0.imprint","IMPRINT",FACE,{"disambiguationData":[TD([[makeQuery(id+"F0.imprint","IMPRINT",EDGE,{"derivedFrom":subQ5}),-1.0]])]});}
            var Q36;
            {var subQ5=sQuery(id+"F0.wireOp",EDGE,"E156.MirrorCS");Q36=makeQuery(id+"F0.imprint","IMPRINT",FACE,{"disambiguationData":[TD([[makeQuery(id+"F0.imprint","IMPRINT",EDGE,{"derivedFrom":subQ5}),1.0]])]});}
            var Q37;
            {var subQ5=sQuery(id+"F0.wireOp",EDGE,"E146.MirrorCS");Q37=makeQuery(id+"F0.imprint","IMPRINT",FACE,{"disambiguationData":[TD([[makeQuery(id+"F0.imprint","IMPRINT",EDGE,{"derivedFrom":subQ5}),-1.0]])]});}
            var Q38;
            {var subQ5=sQuery(id+"F0.wireOp",EDGE,"E142.MirrorCS");Q38=makeQuery(id+"F0.imprint","IMPRINT",FACE,{"disambiguationData":[TD([[makeQuery(id+"F0.imprint","IMPRINT",EDGE,{"derivedFrom":subQ5}),1.0]])]});}
            var Q39;
            {var subQ0=sQuery(id+"F0.wireOp",EDGE,"E62.MirrorCS");Q39=makeQuery(id+"F0.imprint","IMPRINT",FACE,{"disambiguationData":[TD([[makeQuery(id+"F0.imprint","IMPRINT",EDGE,{"derivedFrom":subQ0}),-1.0]])]});}
            var Q40;
            {var subQ0=sQuery(id+"F0.wireOp",EDGE,"E64.MirrorCS");Q40=makeQuery(id+"F0.imprint","IMPRINT",FACE,{"disambiguationData":[TD([[makeQuery(id+"F0.imprint","IMPRINT",EDGE,{"derivedFrom":subQ0}),1.0]])]});}
            var Q41;
            {var subQ0=sQuery(id+"F0.wireOp",EDGE,"E86.left");var subQ1=sQuery(id+"F0.wireOp",EDGE,"E22.MirrorCS");var subQ2=makeQuery(id+"F0.imprint","INTERSECT",VERTEX,{"derivedFrom":[subQ1,subQ0]});Q41=makeQuery(id+"F0.imprint","IMPRINT",FACE,{"disambiguationData":[TD([[makeQuery(id+"F0.imprint","IMPRINT",EDGE,{"disambiguationData":[TD([[subQ2,1.0]])],"derivedFrom":subQ1}),-1.0]])]});}
            var Q42;
            Q42=makeQuery(id+"F2.imprint","IMPRINT",FACE,{"disambiguationData":[TD([[makeQuery(id+"F2.imprint","IMPRINT",EDGE,{"derivedFrom":sQuery(id+"F2.wireOp",EDGE,"E163.bottom")}),-1.0]])]});
            var Q43;
            {var subQ21=sQuery(id+"F0.wireOp",EDGE,"E62.MirrorCS");Q43=makeQuery(id+"F0.imprint","IMPRINT",FACE,{"disambiguationData":[TD([[makeQuery(id+"F0.imprint","IMPRINT",EDGE,{"derivedFrom":subQ21}),1.0]])]});}
            var Q44;
            Q44=makeQuery(id+"F2.imprint","IMPRINT",FACE,{"disambiguationData":[TD([[makeQuery(id+"F2.imprint","IMPRINT",EDGE,{"derivedFrom":sQuery(id+"F2.wireOp",EDGE,"hMRuAE1m-Uf1G-pVpt-2sQ3-avFeiw0Rvket.bottom")}),-1.0]])]});
            extrude(context, id + "F1", {"entities" : qUnion([Q0, Q1, Q2, Q3, Q4, Q5, Q6, Q7, Q8, Q9, Q10, Q11, Q12, Q13, Q14, Q15, Q16, Q17, Q18, Q19, Q20, Q21, Q22, Q23, Q24, Q25, Q26, Q27, Q28, Q29, Q30, Q31, Q32, Q33, Q34, Q35, Q36, Q37, Q38, Q39, Q40, Q41, Q42, Q43, Q44]), "depth" : 3 * mm, "offsetDistance" : 25 * mm});
        }
        {
            var Q0;
            Q0=qCreatedBy(makeId("Top.planeOp"),FACE);
            var sketch = newSketch(context, id + "F2", { "sketchPlane" : qUnion([Q0])});
            skLineSegment(sketch, "E163.bottom", {"start": v(31.77, -6.13) * mm, "end": v(26.77, -6.13) * mm});
            skLineSegment(sketch, "E163.top", {"start": v(31.77, 8.87) * mm, "end": v(26.77, 8.87) * mm});
            skLineSegment(sketch, "E163.left", {"start": v(31.77, -6.13) * mm, "end": v(31.77, 8.87) * mm});
            skLineSegment(sketch, "E163.right", {"start": v(26.77, -6.13) * mm, "end": v(26.77, 8.87) * mm});
            skPoint(sketch, "E163.middle", {"position": v(29.27, 1.37) * mm});
            skSolve(sketch);
        }
        {
            var Q0;
            Q0=qSketchRegion(id+"F2",true);
            extrude(context, id + "F3", {"entities" : qUnion([Q0]), "operationType" : NewBodyOperationType.REMOVE, "depth" : 25 * mm, "offsetDistance" : 25 * mm});
        }
    });
